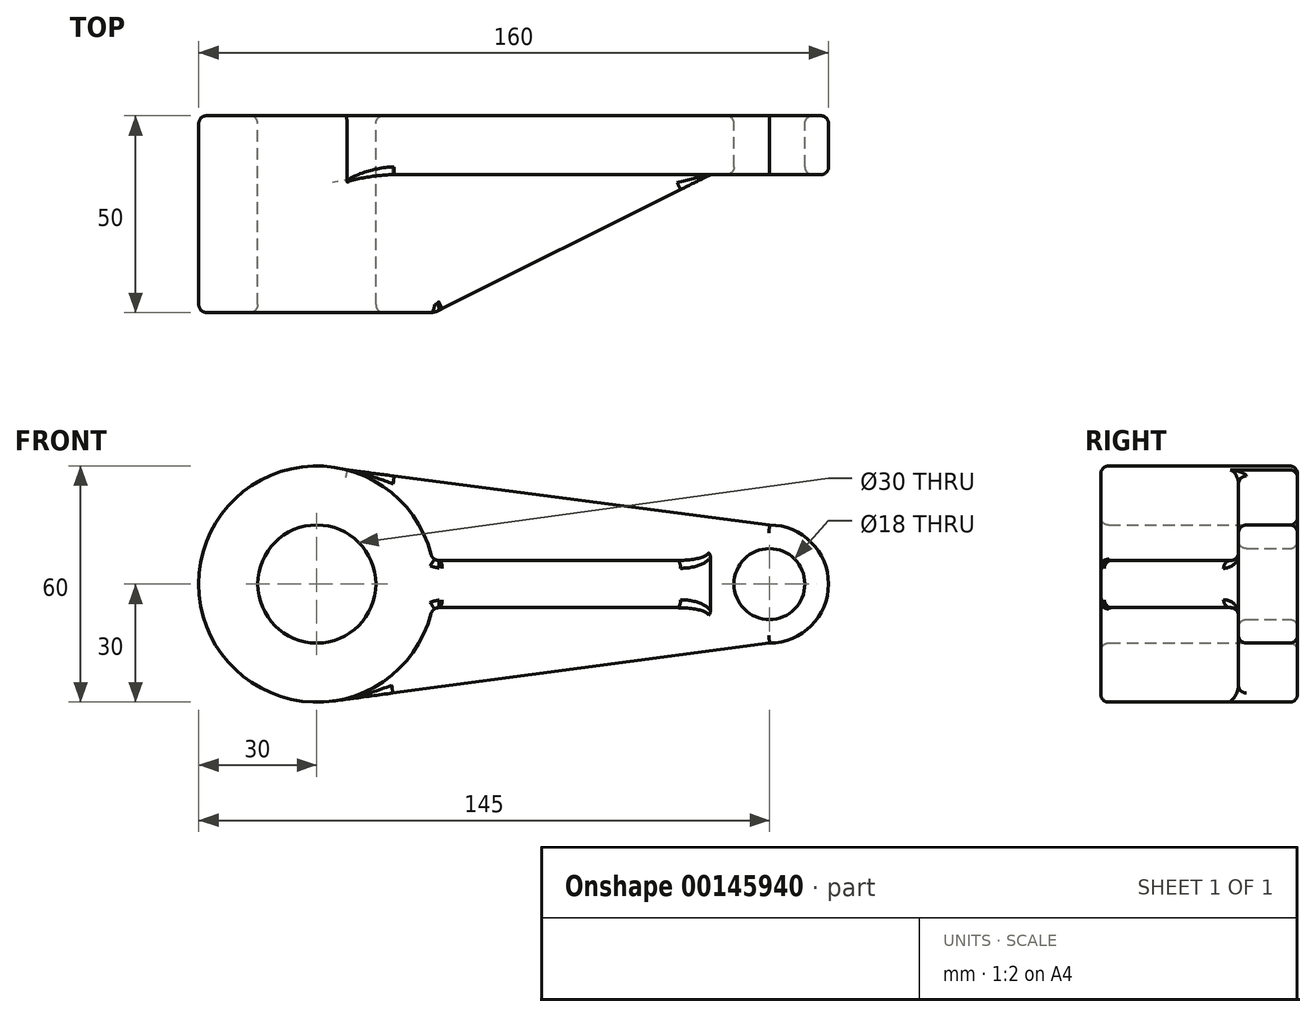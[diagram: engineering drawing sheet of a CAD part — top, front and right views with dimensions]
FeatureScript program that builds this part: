
annotation { "Feature Type Name" : "Feature", "Feature Type Description" : "" }
export const myFeature = defineFeature(function(context is Context, id is Id, definition is map)
    precondition{}
    {
        {
            var Q0;
            Q0=qCreatedBy(makeId("Front.planeOp"),FACE);
            var sketch = newSketch(context, id + "F0", { "sketchPlane" : qUnion([Q0])});
            skCircle(sketch, "E0", {"center": v(0, 0) * mm, "radius": 30 * mm});
            skCircle(sketch, "E1", {"center": v(0, 0) * mm, "radius": 15 * mm});
            skSolve(sketch);
        }
        {
            var Q0;
            Q0=makeQuery(id+"F0.imprint","IMPRINT",FACE,{"disambiguationData":[TD([[makeQuery(id+"F0.imprint","IMPRINT",EDGE,{"derivedFrom":sQuery(id+"F0.wireOp",EDGE,"E0")}),1.0]])]});
            extrude(context, id + "F1", {"entities" : qUnion([Q0]), "depth" : 50 * mm});
        }
        {
            var Q0;
            Q0=qCreatedBy(makeId("Front.planeOp"),FACE);
            var sketch = newSketch(context, id + "F2", { "sketchPlane" : qUnion([Q0])});
            skCircle(sketch, "E2", {"center": v(115, 0) * mm, "radius": 9 * mm});
            skCircle(sketch, "E3", {"center": v(115, 0) * mm, "radius": 15 * mm});
            skSolve(sketch);
        }
        {
            var Q0;
            Q0=makeQuery(id+"F2.imprint","IMPRINT",FACE,{"disambiguationData":[TD([[makeQuery(id+"F2.imprint","IMPRINT",EDGE,{"derivedFrom":sQuery(id+"F2.wireOp",EDGE,"E2")}),-1.0]])]});
            extrude(context, id + "F3", {"entities" : qUnion([Q0]), "depth" : 15 * mm});
        }
        {
            var Q0;
            Q0=makeQuery(id+"F1.opExtrude","CAP_FACE",FACE,{"disambiguationData":[OSD([sQuery(id+"F0.wireOp",EDGE,"E0"),sQuery(id+"F0.wireOp",EDGE,"E1")])],"isStart":true});
            var sketch = newSketch(context, id + "F4", { "sketchPlane" : qUnion([Q0])});
            skArc(sketch, "E4.0", {"start": v(-115, -15) * mm, "mid": v(-100, 0) * mm, "end": v(-115, 15) * mm});
            skArc(sketch, "E4.1", {"start": v(0, 30) * mm, "mid": v(-29.93, 1.98) * mm, "end": v(-3.95, -29.74) * mm});
            skLineSegment(sketch, "E5", {"start": v(-115, 15) * mm, "end": v(0, 30) * mm});
            skLineSegment(sketch, "E6", {"start": v(-115, -15) * mm, "end": v(0, -30.26) * mm});
            skSolve(sketch);
        }
        {
            var Q0;
            {var subQ0=sQuery(id+"F4.wireOp",EDGE,"E4.0");Q0=makeQuery(id+"F4.imprint","IMPRINT",FACE,{"disambiguationData":[TD([[makeQuery(id+"F4.imprint","IMPRINT",EDGE,{"derivedFrom":subQ0}),-1.0]])]});}
            extrude(context, id + "F5", {"entities" : qUnion([Q0]), "oppositeDirection" : true, "depth" : 15 * mm});
        }
        {
            var Q0;
            Q0=qCreatedBy(makeId("Top.planeOp"),FACE);
            var sketch = newSketch(context, id + "F6", { "sketchPlane" : qUnion([Q0])});
            skLineSegment(sketch, "E7.0", {"start": v(30, -50) * mm, "end": v(-30, -50) * mm, "construction": true});
            skLineSegment(sketch, "E8.0", {"start": v(115, -15) * mm, "end": v(3.95, -15) * mm, "construction": true});
            skLineSegment(sketch, "E9", {"start": v(21.88, -50) * mm, "end": v(30, -50) * mm});
            skLineSegment(sketch, "E10", {"start": v(30, -50) * mm, "end": v(100, -15) * mm});
            skLineSegment(sketch, "E11", {"start": v(100, -15) * mm, "end": v(21.88, -15) * mm});
            skLineSegment(sketch, "E12", {"start": v(21.88, -15) * mm, "end": v(21.88, -50) * mm});
            skSolve(sketch);
        }
        {
            var Q0;
            Q0=makeQuery(id+"F6.imprint","IMPRINT",FACE,{"disambiguationData":[TD([[makeQuery(id+"F6.imprint","IMPRINT",EDGE,{"derivedFrom":sQuery(id+"F6.wireOp",EDGE,"E9")}),1.0]])]});
            extrude(context, id + "F7", {"entities" : qUnion([Q0]), "operationType" : NewBodyOperationType.ADD, "endBound" : BoundingType.SYMMETRIC, "depth" : 12 * mm});
        }
        {
            var Q0;
            Q0=makeQuery(id+"F7.opExtrude","SWEPT_EDGE",EDGE,{"disambiguationData":[OSD([sQuery(id+"F6.wireOp",EDGE,"E9"),sQuery(id+"F6.wireOp",EDGE,"E10")])]});
            fillet(context, id + "F8", {"entities" : qUnion([Q0]), "radius" : 5 * mm, "tangentPropagation" : true, "allowEdgeOverflow" : false});
        }
        {
            var Q0;
            Q0=makeQuery(id+"F7.boolean.opBoolean","INTERSECT",EDGE,{"derivedFrom":[makeQuery(id+"F1.opExtrude","SWEPT_FACE",FACE,{"disambiguationData":[OSD([sQuery(id+"F0.wireOp",EDGE,"E0")])]}),makeQuery(id+"F7.opExtrude","CAP_FACE",FACE,{"disambiguationData":[OSD([sQuery(id+"F6.wireOp",EDGE,"E9"),sQuery(id+"F6.wireOp",EDGE,"E10"),sQuery(id+"F6.wireOp",EDGE,"E11"),sQuery(id+"F6.wireOp",EDGE,"E12")])],"isStart":true})]});
            var Q1;
            Q1=makeQuery(id+"F7.boolean.opBoolean","INTERSECT",EDGE,{"derivedFrom":[makeQuery(id+"F1.opExtrude","SWEPT_FACE",FACE,{"disambiguationData":[OSD([sQuery(id+"F0.wireOp",EDGE,"E0")])]}),makeQuery(id+"F7.opExtrude","CAP_FACE",FACE,{"disambiguationData":[OSD([sQuery(id+"F6.wireOp",EDGE,"E9"),sQuery(id+"F6.wireOp",EDGE,"E10"),sQuery(id+"F6.wireOp",EDGE,"E11"),sQuery(id+"F6.wireOp",EDGE,"E12")])],"isStart":false})]});
            fillet(context, id + "F9", {"entities" : qUnion([Q0, Q1]), "radius" : 2 * mm, "tangentPropagation" : true, "allowEdgeOverflow" : false});
        }
        {
            var Q0;
            Q0=makeQuery(id+"F7.opExtrude","CAP_EDGE",EDGE,{"disambiguationData":[OSD([sQuery(id+"F6.wireOp",EDGE,"E11")])],"isStart":true});
            var Q1;
            Q1=makeQuery(id+"F7.opExtrude","CAP_EDGE",EDGE,{"disambiguationData":[OSD([sQuery(id+"F6.wireOp",EDGE,"E11")])],"isStart":false});
            fillet(context, id + "F10", {"entities" : qUnion([Q0, Q1]), "radius" : 2 * mm, "tangentPropagation" : true, "allowEdgeOverflow" : false});
        }
        {
            var Q0;
            Q0=makeQuery(id+"F5.opExtrude","CAP_EDGE",EDGE,{"disambiguationData":[OSD([sQuery(id+"F4.wireOp",EDGE,"E6")])],"isStart":true});
            var Q1;
            Q1=makeQuery(id+"F5.opExtrude","CAP_EDGE",EDGE,{"disambiguationData":[OSD([sQuery(id+"F4.wireOp",EDGE,"E5")])],"isStart":true});
            var Q2;
            Q2=makeQuery(id+"F1.opExtrude","CAP_EDGE",EDGE,{"disambiguationData":[OSD([sQuery(id+"F0.wireOp",EDGE,"E0")])],"isStart":true});
            var Q3;
            Q3=makeQuery(id+"F3.opExtrude","CAP_EDGE",EDGE,{"disambiguationData":[OSD([sQuery(id+"F2.wireOp",EDGE,"E3")])],"isStart":true});
            var Q4;
            Q4=makeQuery(id+"F5.opExtrude","CAP_EDGE",EDGE,{"disambiguationData":[OSD([sQuery(id+"F4.wireOp",EDGE,"E6")])],"isStart":false});
            var Q5;
            Q5=makeQuery(id+"F5.opExtrude","CAP_EDGE",EDGE,{"disambiguationData":[OSD([sQuery(id+"F4.wireOp",EDGE,"E5")])],"isStart":false});
            var Q6;
            Q6=makeQuery(id+"F3.opExtrude","CAP_EDGE",EDGE,{"disambiguationData":[OSD([sQuery(id+"F2.wireOp",EDGE,"E3")])],"isStart":false});
            fillet(context, id + "F11", {"entities" : qUnion([Q0, Q1, Q2, Q3, Q4, Q5, Q6]), "radius" : 2 * mm, "tangentPropagation" : true, "allowEdgeOverflow" : false});
        }
        {
            var Q0;
            Q0=makeQuery(id+"F3.opExtrude","CAP_EDGE",EDGE,{"disambiguationData":[OSD([sQuery(id+"F2.wireOp",EDGE,"E2")])],"isStart":false});
            var Q1;
            Q1=makeQuery(id+"F1.opExtrude","CAP_EDGE",EDGE,{"disambiguationData":[OSD([sQuery(id+"F0.wireOp",EDGE,"E1")])],"isStart":false});
            var Q2;
            Q2=makeQuery(id+"F1.opExtrude","CAP_EDGE",EDGE,{"disambiguationData":[OSD([sQuery(id+"F0.wireOp",EDGE,"E0")])],"isStart":false});
            var Q3;
            Q3=makeQuery(id+"F1.opExtrude","CAP_EDGE",EDGE,{"disambiguationData":[OSD([sQuery(id+"F0.wireOp",EDGE,"E1")])],"isStart":true});
            var Q4;
            Q4=makeQuery(id+"F3.opExtrude","CAP_EDGE",EDGE,{"disambiguationData":[OSD([sQuery(id+"F2.wireOp",EDGE,"E2")])],"isStart":true});
            fillet(context, id + "F12", {"entities" : qUnion([Q0, Q1, Q2, Q3, Q4]), "radius" : 2 * mm, "tangentPropagation" : true, "allowEdgeOverflow" : false});
        }
    });
